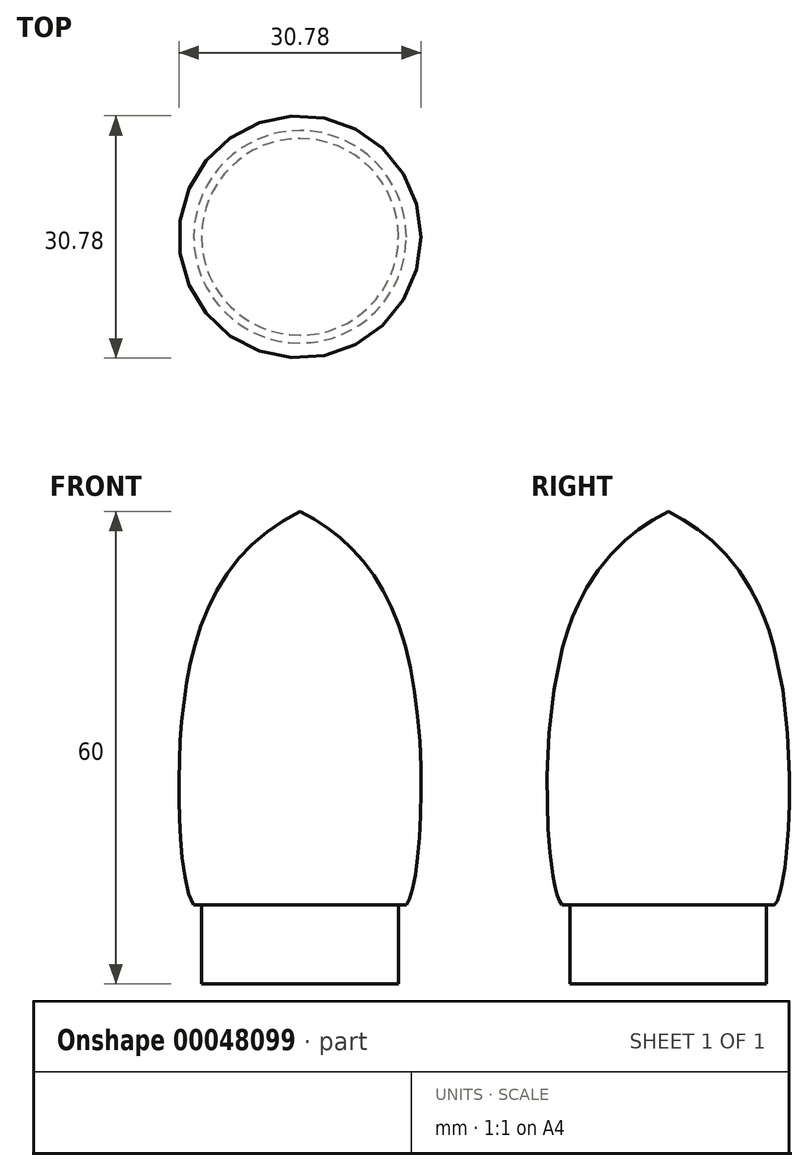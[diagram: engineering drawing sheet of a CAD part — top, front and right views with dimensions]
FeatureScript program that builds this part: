
annotation { "Feature Type Name" : "Feature", "Feature Type Description" : "" }
export const myFeature = defineFeature(function(context is Context, id is Id, definition is map)
    precondition{}
    {
        {
            var Q0;
            Q0=qCreatedBy(makeId("Front.planeOp"),FACE);
            var sketch = newSketch(context, id + "F0", { "sketchPlane" : qUnion([Q0])});
            skLineSegment(sketch, "E0", {"start": v(0, 60) * mm, "end": v(0, 0) * mm});
            skLineSegment(sketch, "E1", {"start": v(0, 0) * mm, "end": v(12.5, 0) * mm});
            skLineSegment(sketch, "E2", {"start": v(12.5, 0) * mm, "end": v(12.5, 10) * mm});
            skLineSegment(sketch, "E3", {"start": v(12.5, 10) * mm, "end": v(13.5, 10) * mm});
            skFitSpline(sketch, "E4", {"points": [v(0, 60) * mm, v(13.9, 40.85) * mm, v(13.5, 10) * mm, v(12.5, 10) * mm], "startDerivative": vector(46.03, -22.52) * mm, "endDerivative": vector(-11.33, 6.3) * mm});
            skSolve(sketch);
        }
        {
            var Q0;
            {var subQ2=sQuery(id+"F0.wireOp",EDGE,"E0");Q0=makeQuery(id+"F0.imprint","IMPRINT",FACE,{"disambiguationData":[TD([[makeQuery(id+"F0.imprint","IMPRINT",EDGE,{"derivedFrom":subQ2}),1.0]])]});}
            var Q1;
            Q1=sQuery(id+"F0.wireOp",EDGE,"E0");
            revolve(context, id + "F1", {"entities" : qUnion([Q0]), "axis" : qUnion([Q1]), "revolveType" : RevolveType.FULL});
        }
    });
